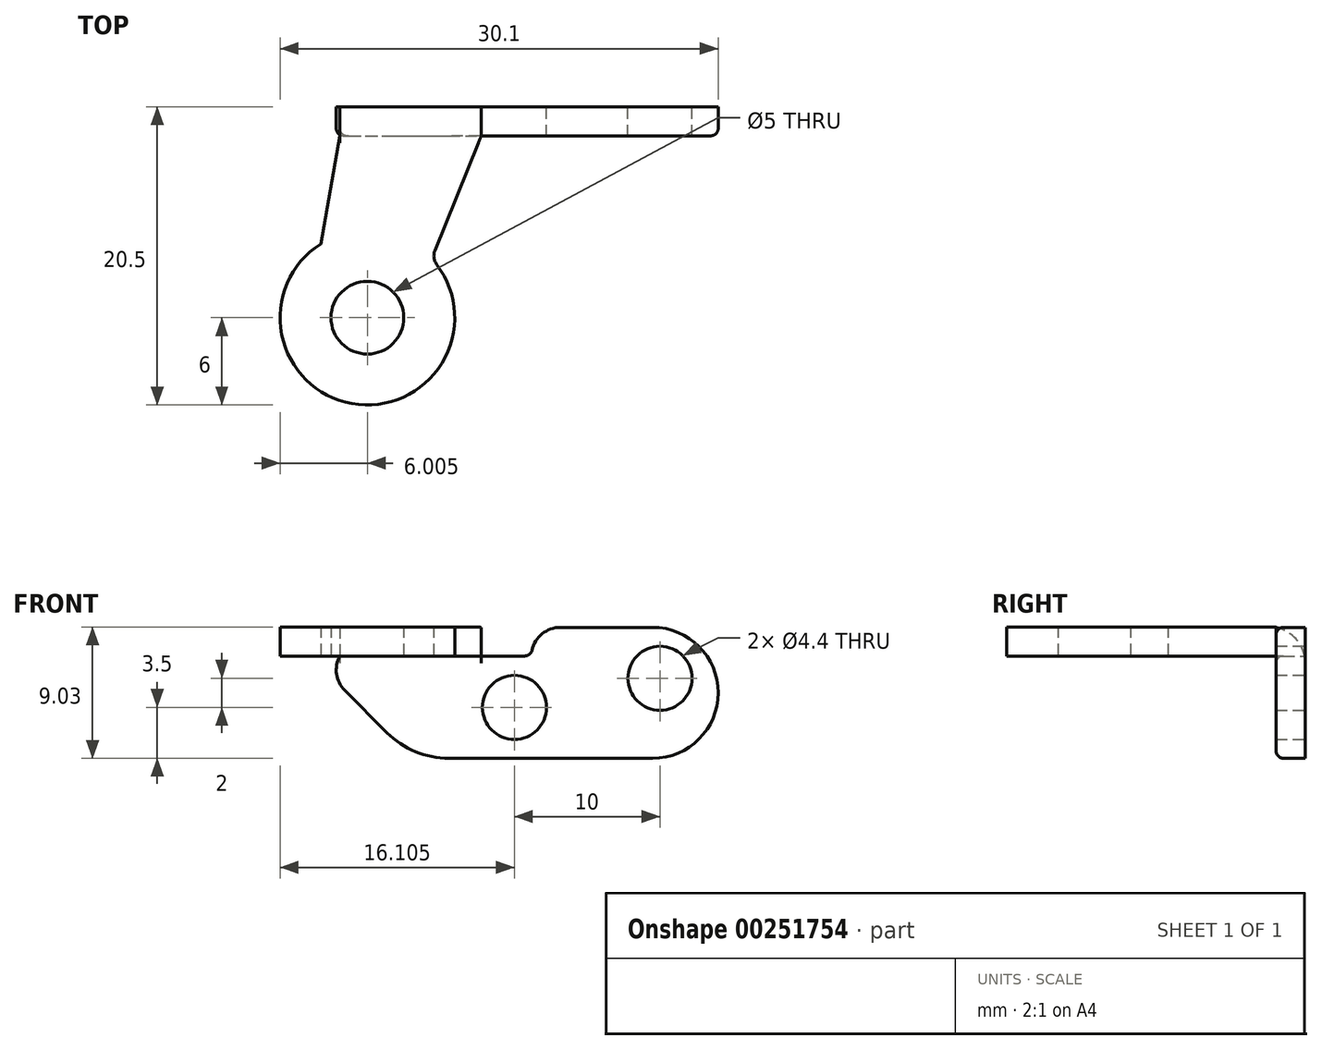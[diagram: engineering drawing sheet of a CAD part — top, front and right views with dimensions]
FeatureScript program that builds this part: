
annotation { "Feature Type Name" : "Feature", "Feature Type Description" : "" }
export const myFeature = defineFeature(function(context is Context, id is Id, definition is map)
    precondition{}
    {
        {
            var Q0;
            Q0=qCreatedBy(makeId("Front.planeOp"),FACE);
            var sketch = newSketch(context, id + "F0", { "sketchPlane" : qUnion([Q0])});
            skArc(sketch, "E0", {"start": v(8.46, -4.5) * mm, "mid": v(12.96, 0) * mm, "end": v(8.46, 4.5) * mm});
            skLineSegment(sketch, "E1", {"start": v(8.46, -4.5) * mm, "end": v(-5.54, -4.5) * mm});
            skLineSegment(sketch, "E2", {"start": v(8.46, 4.5) * mm, "end": v(2.13, 4.5) * mm});
            skLineSegment(sketch, "E3", {"start": v(0.13, 2.5) * mm, "end": v(0.13, 2.5) * mm});
            skLineSegment(sketch, "E4", {"start": v(-0.31, 2.53) * mm, "end": v(-13.04, 2.53) * mm});
            skLineSegment(sketch, "E5", {"start": v(-12.69, 0.17) * mm, "end": v(-9.78, -2.74) * mm});
            skPoint(sketch, "E6", {"position": v(8.96, 1) * mm});
            skPoint(sketch, "E7.visualSharp", {"position": v(-8.02, -4.5) * mm});
            skArc(sketch, "E7.filletArc", {"start": v(-9.78, -2.74) * mm, "mid": v(-7.83, -4.04) * mm, "end": v(-5.54, -4.5) * mm});
            skPoint(sketch, "E8.visualSharp", {"position": v(0.13, 4.5) * mm});
            skArc(sketch, "E8.filletArc", {"start": v(2.13, 4.5) * mm, "mid": v(0.87, 4.06) * mm, "end": v(0.18, 2.93) * mm});
            skArc(sketch, "E9.filletArc", {"start": v(0.13, 2.52) * mm, "mid": v(0.13, 2.5) * mm, "end": v(0.13, 2.5) * mm});
            skArc(sketch, "E10.filletArc", {"start": v(-0.31, 2.53) * mm, "mid": v(0, 2.64) * mm, "end": v(0.18, 2.93) * mm});
            skArc(sketch, "E11", {"start": v(-13.04, 2.53) * mm, "mid": v(-13.25, 1.3) * mm, "end": v(-12.69, 0.17) * mm});
            skPoint(sketch, "E12.endSnap0", {"position": v(12.96, 14.18) * mm});
            skPoint(sketch, "E13", {"position": v(-1.04, -1) * mm});
            skPoint(sketch, "E14.trimOffspring.end.orphan", {"position": v(12.96, -25.2) * mm});
            skPoint(sketch, "E14.trimOffspring.start.orphan", {"position": v(12.96, 0) * mm});
            skPoint(sketch, "E15.end.orphan", {"position": v(12.96, 28.37) * mm});
            skSolve(sketch);
        }
        {
            var Q0;
            Q0 = qSketchRegion(id + "F0", true);
            extrude(context, id + "F1", {"entities" : qUnion([Q0]), "depth" : 2 * mm});
        }
        {
            var Q0;
            Q0=sQuery(id+"F0.wireOp",VERTEX,"E13");
            var Q1;
            Q1=sQuery(id+"F0.wireOp",VERTEX,"E6");
            var Q2;
            Q2=makeQuery(id+"F1.opExtrude","SWEPT_BODY",BODY,{"disambiguationData":[OSD([sQuery(id+"F0.wireOp",EDGE,"E0"),sQuery(id+"F0.wireOp",EDGE,"E1"),sQuery(id+"F0.wireOp",EDGE,"E2"),sQuery(id+"F0.wireOp",EDGE,"E4"),sQuery(id+"F0.wireOp",EDGE,"E5"),sQuery(id+"F0.wireOp",EDGE,"E7.filletArc"),sQuery(id+"F0.wireOp",EDGE,"E8.filletArc"),sQuery(id+"F0.wireOp",EDGE,"E10.filletArc"),sQuery(id+"F0.wireOp",EDGE,"E11")])]});
            hole(context, id + "F2", {"style" : HoleStyle.SIMPLE, "endStyle" : HoleEndStyle.THROUGH, "oppositeDirection" : true, "standardTappedOrClearance" : lookupTablePath({ "standard" : "ISO", "fit" : "Normal", "size" : "M4", "type" : "Clearance" }), "standardBlindInLast" : lookupTablePath({ "fit" : "Standard", "standard" : "ISO", "size" : "M4", "type" : "Clearance" }), "holeDiameter" : 4.4 * mm, "isTappedThrough" : true, "tappedDepth" : 12 * mm, "tapClearance" : 3, "locations" : qUnion([Q0, Q1]), "scope" : qUnion([Q2])});
        }
        {
            var Q0;
            Q0=makeQuery(id+"F1.opExtrude","CAP_FACE",FACE,{"disambiguationData":[OSD([sQuery(id+"F0.wireOp",EDGE,"E0"),sQuery(id+"F0.wireOp",EDGE,"E1"),sQuery(id+"F0.wireOp",EDGE,"E2"),sQuery(id+"F0.wireOp",EDGE,"E4"),sQuery(id+"F0.wireOp",EDGE,"E5"),sQuery(id+"F0.wireOp",EDGE,"E7.filletArc"),sQuery(id+"F0.wireOp",EDGE,"E8.filletArc"),sQuery(id+"F0.wireOp",EDGE,"E10.filletArc"),sQuery(id+"F0.wireOp",EDGE,"E11")])],"isStart":true});
            var sketch = newSketch(context, id + "F3", { "sketchPlane" : qUnion([Q0])});
            skLineSegment(sketch, "E16.top", {"start": v(17.14, 4.53) * mm, "end": v(3.31, 4.53) * mm});
            skLineSegment(sketch, "E16.right", {"start": v(3.31, 2.53) * mm, "end": v(3.31, 4.53) * mm});
            skPoint(sketch, "E17.orphan", {"position": v(0.31, 2.53) * mm});
            skPoint(sketch, "E18.0.2.start.orphan", {"position": v(13.04, 2.53) * mm});
            skLineSegment(sketch, "E19", {"start": v(3.31, 2.53) * mm, "end": v(17.14, 2.53) * mm});
            skLineSegment(sketch, "E20", {"start": v(17.14, 2.53) * mm, "end": v(17.14, 4.53) * mm});
            skPoint(sketch, "E21.0.center.orphan", {"position": v(-8.96, 1) * mm});
            skSolve(sketch);
        }
        {
            var Q0;
            Q0 = qSketchRegion(id + "F3", true);
            extrude(context, id + "F4", {"entities" : qUnion([Q0]), "operationType" : NewBodyOperationType.ADD, "oppositeDirection" : true, "depth" : 20.5 * mm});
        }
        {
            var Q0;
            Q0=makeQuery(id+"F4.opExtrude","SWEPT_FACE",FACE,{"disambiguationData":[OSD([sQuery(id+"F3.wireOp",EDGE,"E19")])]});
            var sketch = newSketch(context, id + "F5", { "sketchPlane" : qUnion([Q0])});
            skCircle(sketch, "E22", {"center": v(-11.14, 14.5) * mm, "radius": 2.5 * mm});
            skLineSegment(sketch, "E23.0", {"start": v(11.16, 2) * mm, "end": v(6.76, 2) * mm});
            skPoint(sketch, "E24", {"position": v(8.96, 2) * mm});
            skLineSegment(sketch, "E25.0", {"start": v(-13.04, 0) * mm, "end": v(-17.14, 0) * mm});
            skCircle(sketch, "E26", {"center": v(-11.14, 14.5) * mm, "radius": 6 * mm});
            skLineSegment(sketch, "E27", {"start": v(-13.04, 2) * mm, "end": v(-14.35, 9.43) * mm});
            skLineSegment(sketch, "E28", {"start": v(-3.31, 2) * mm, "end": v(-6.72, 10.44) * mm});
            skLineSegment(sketch, "E29.0.0", {"start": v(-13.04, 0) * mm, "end": v(-13.04, 2) * mm});
            skLineSegment(sketch, "E29.0.1", {"start": v(-13.04, 2) * mm, "end": v(-3.31, 2) * mm});
            skLineSegment(sketch, "E29.0.2", {"start": v(-3.31, 2) * mm, "end": v(-3.31, 20.5) * mm});
            skLineSegment(sketch, "E29.0.3", {"start": v(-3.31, 20.5) * mm, "end": v(-17.14, 20.5) * mm});
            skLineSegment(sketch, "E29.0.4", {"start": v(-17.14, 20.5) * mm, "end": v(-17.14, 0) * mm});
            skLineSegment(sketch, "E29.0.5", {"start": v(-17.14, 0) * mm, "end": v(-13.04, 0) * mm});
            skSolve(sketch);
        }
        {
            var Q0;
            {var subQ0=sQuery(id+"F5.wireOp",EDGE,"E28");Q0=makeQuery(id+"F5.imprint","IMPRINT",FACE,{"disambiguationData":[TD([[makeQuery(id+"F5.imprint","IMPRINT",EDGE,{"derivedFrom":subQ0}),-1.0]])]});}
            var Q1;
            {var subQ0=sQuery(id+"F5.wireOp",EDGE,"E29.0.4");var subQ1=sQuery(id+"F5.wireOp",EDGE,"E26");var subQ2=makeQuery(id+"F5.imprint","INTERSECT",VERTEX,{"derivedFrom":[subQ1,subQ0]});Q1=makeQuery(id+"F5.imprint","IMPRINT",FACE,{"disambiguationData":[TD([[makeQuery(id+"F5.imprint","IMPRINT",EDGE,{"disambiguationData":[TD([[subQ2,1.0]])],"derivedFrom":subQ1}),-1.0]])]});}
            var Q2;
            {var subQ4=sQuery(id+"F5.wireOp",EDGE,"E27");Q2=makeQuery(id+"F5.imprint","IMPRINT",FACE,{"disambiguationData":[TD([[makeQuery(id+"F5.imprint","IMPRINT",EDGE,{"derivedFrom":subQ4}),1.0]])]});}
            var Q3;
            Q3=makeQuery(id+"F5.imprint","IMPRINT",FACE,{"disambiguationData":[TD([[makeQuery(id+"F5.imprint","IMPRINT",EDGE,{"derivedFrom":sQuery(id+"F5.wireOp",EDGE,"E22")}),1.0]])]});
            extrude(context, id + "F6", {"entities" : qUnion([Q0, Q1, Q2, Q3]), "operationType" : NewBodyOperationType.REMOVE, "oppositeDirection" : true, "depth" : 25 * mm});
        }
        {
            var Q0;
            Q0=makeQuery(id+"F6.boolean.opBoolean","COPY",EDGE,{"derivedFrom":makeQuery(id+"F6.opExtrude","SWEPT_EDGE",EDGE,{"disambiguationData":[OSD([sQuery(id+"F5.wireOp",EDGE,"E26"),sQuery(id+"F5.wireOp",EDGE,"E28")])]})});
            fillet(context, id + "F7", {"entities" : qUnion([Q0]), "radius" : 1 * mm, "tangentPropagation" : true, "allowEdgeOverflow" : false});
        }
        {
            var Q0;
            {var subQ0=sQuery(id+"F0.wireOp",EDGE,"E4");Q0=makeQuery(id+"F4.boolean.opBoolean","SPLIT",EDGE,{"disambiguationData":[topologyDisambiguationEdgeConnected([makeQuery(id+"F4.opExtrude","SWEPT_FACE",FACE,{"disambiguationData":[OSD([sQuery(id+"F3.wireOp",EDGE,"E19")])]})])],"derivedFrom":makeQuery(id+"F1.opExtrude","CAP_EDGE",EDGE,{"disambiguationData":[OSD([subQ0])],"isStart":false})});}
            fillet(context, id + "F8", {"entities" : qUnion([Q0]), "radius" : 0.5 * mm, "tangentPropagation" : true, "allowEdgeOverflow" : false});
        }
        {
            var Q0;
            Q0=makeQuery(id+"F6.boolean.opBoolean","COPY",FACE,{"derivedFrom":makeQuery(id+"F6.opExtrude","SWEPT_FACE",FACE,{"disambiguationData":[OSD([sQuery(id+"F5.wireOp",EDGE,"E29.0.0")])]})});
            var sketch = newSketch(context, id + "F9", { "sketchPlane" : qUnion([Q0])});
            skLineSegment(sketch, "E30.0", {"start": v(2, 4.53) * mm, "end": v(2.5, 4.53) * mm});
            skLineSegment(sketch, "E31.0", {"start": v(0, 2.53) * mm, "end": v(0, 2.03) * mm});
            skPoint(sketch, "E32.visualSharp", {"position": v(0, 4.53) * mm});
            skArc(sketch, "E32.filletArc", {"start": v(2.5, 4.53) * mm, "mid": v(0.73, 3.8) * mm, "end": v(0, 2.03) * mm});
            skLineSegment(sketch, "E33", {"start": v(2.5, 4.53) * mm, "end": v(0, 4.53) * mm});
            skLineSegment(sketch, "E34", {"start": v(0, 2.03) * mm, "end": v(0, 4.53) * mm});
            skSolve(sketch);
        }
        {
            var Q0;
            Q0 = qSketchRegion(id + "F9", true);
            var Q1;
            Q1=makeQuery(id+"F4.opExtrude","SWEPT_FACE",FACE,{"disambiguationData":[OSD([sQuery(id+"F3.wireOp",EDGE,"E16.right")])]});
            extrude(context, id + "F10", {"entities" : qUnion([Q0]), "operationType" : NewBodyOperationType.REMOVE, "endBound" : BoundingType.UP_TO_SURFACE, "oppositeDirection" : true, "endBoundEntityFace" : qUnion([Q1]), "depth" : 25 * mm});
        }
    });
